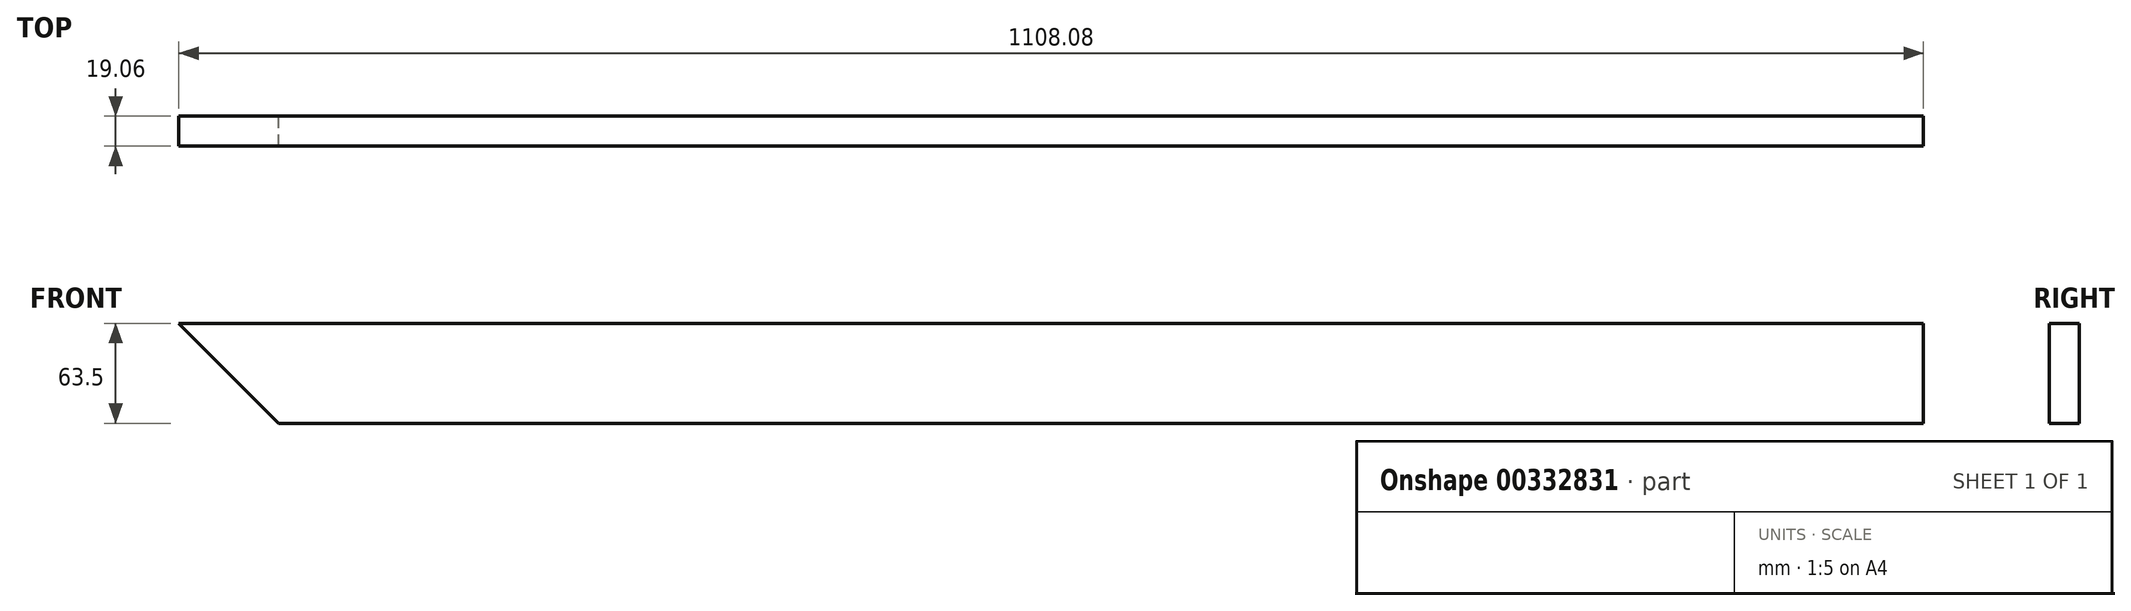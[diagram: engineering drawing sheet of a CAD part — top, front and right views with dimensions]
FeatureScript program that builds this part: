
annotation { "Feature Type Name" : "Feature", "Feature Type Description" : "" }
export const myFeature = defineFeature(function(context is Context, id is Id, definition is map)
    precondition{}
    {
        {
            var Q0;
            Q0=qCreatedBy(makeId("Front.planeOp"),FACE);
            var sketch = newSketch(context, id + "F0", { "sketchPlane" : qUnion([Q0])});
            skLineSegment(sketch, "E0.bottom", {"start": v(554.04, 31.75) * mm, "end": v(-554.04, 31.75) * mm});
            skLineSegment(sketch, "E0.top", {"start": v(554.04, -31.75) * mm, "end": v(-490.54, -31.75) * mm});
            skLineSegment(sketch, "E0.left", {"start": v(554.04, 31.75) * mm, "end": v(554.04, -31.75) * mm});
            skPoint(sketch, "E0.middle", {"position": v(0, 0) * mm});
            skPoint(sketch, "E0.right.start.orphan", {"position": v(-554.04, 31.75) * mm});
            skLineSegment(sketch, "E1", {"start": v(-554.04, 31.75) * mm, "end": v(-490.54, -31.75) * mm});
            skPoint(sketch, "E2.orphan", {"position": v(-554.04, -31.75) * mm});
            skSolve(sketch);
        }
        {
            var Q0;
            Q0=makeQuery(id+"F0.imprint","IMPRINT",FACE,{"disambiguationData":[TD([[makeQuery(id+"F0.imprint","IMPRINT",EDGE,{"derivedFrom":sQuery(id+"F0.wireOp",EDGE,"E0.bottom")}),1.0]])]});
            extrude(context, id + "F1", {"entities" : qUnion([Q0]), "endBound" : BoundingType.SYMMETRIC, "depth" : 19.05 * mm});
        }
    });
